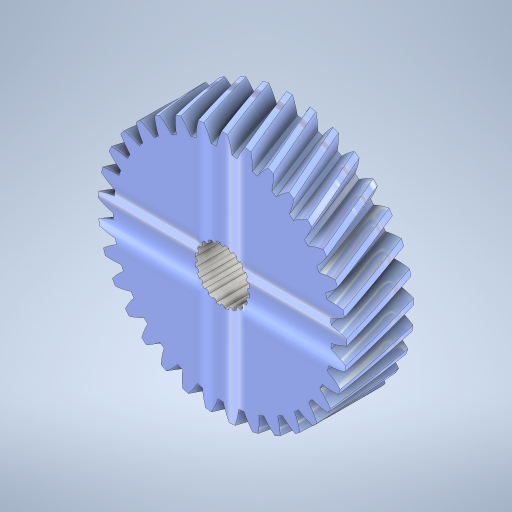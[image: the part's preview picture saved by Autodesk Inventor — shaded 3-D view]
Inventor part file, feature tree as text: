
AUTODESK INVENTOR PART (.ipt)
format: ipt  version: 2024 (Build 280153000, 153)  size: 863,232 bytes
history: native  units: mm (DEFAULTED — no unit token found)
features: plane x3, other x3, extrude x2, sketch x1
ambient origin geometry x8: Origin, YZ Plane, XZ Plane, XY Plane, X Axis, Y Axis, Z Axis, Center Point
bodies: Solid1 (feature_tree)
feature tree (9):
  extrude  "Extrusion1"  Depth=15.0mm TaperAngle=0.0deg
  plane  "Work Plane2"
  plane  "Work Plane8"
  plane  "Work Plane9"
  other  "Spur Gear"
  extrude  "Extrusion2"  Depth=0.515mm
  sketch  "Sketch1"  dims[d0=55.676444mm d1=15.0mm d2=0.0mm d3=52.6768mm d4=10.0mm d5=0.0mm d16=63.909111mm d17=0.0mm d34=0.951998mm d39=0.0mm d41=0.0mm d43=63.909111mm d46=63.909111mm d47=0.0mm d48=0.0mm d49=12.217mm d50=0.0mm d51=0.0mm d53=0.515mm d54=6.1135mm d55=200.0mm d57=360.0deg d59=0.5mm d60=0.872665mm d61=0.5mm d62=0.872665mm]
  other  "Srf1"
  other  "Pitch Diameter"
